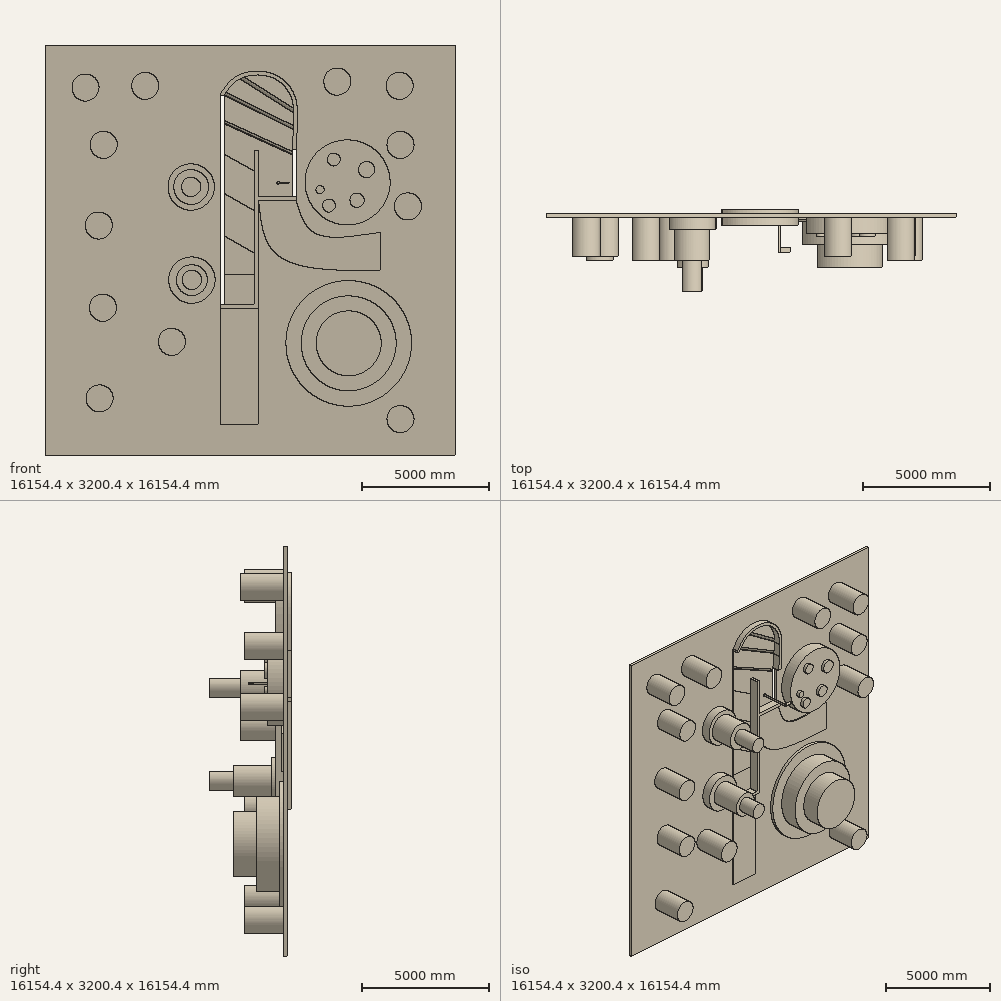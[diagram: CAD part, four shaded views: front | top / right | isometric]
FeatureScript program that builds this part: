
annotation { "Feature Type Name" : "Feature", "Feature Type Description" : "" }
export const myFeature = defineFeature(function(context is Context, id is Id, definition is map)
    precondition{}
    {
        {
            var Q0;
            Q0=qCreatedBy(makeId("Front.planeOp"),FACE);
            var sketch = newSketch(context, id + "F0", { "sketchPlane" : qUnion([Q0])});
            skLineSegment(sketch, "E0.bottom", {"start": v(12.17, -69.16) * mm, "end": v(1510.57, -69.16) * mm});
            skLineSegment(sketch, "E0.right", {"start": v(1510.57, -69.16) * mm, "end": v(1510.57, 6026.84) * mm});
            skLineSegment(sketch, "E1.top", {"start": v(1510.57, 4198.04) * mm, "end": v(2993.71, 4198.04) * mm});
            skLineSegment(sketch, "E1.left", {"start": v(1510.57, 6026.84) * mm, "end": v(1510.57, 4198.04) * mm});
            skCircle(sketch, "E2", {"center": v(2297.14, 4738.79) * mm, "radius": 64.77 * mm});
            skLineSegment(sketch, "E3", {"start": v(164.57, -69.16) * mm, "end": v(164.57, 8187.7) * mm});
            skFitSpline(sketch, "E4", {"points": [v(164.57, 8187.7) * mm, v(785.27, 8827.79) * mm, v(1987.86, 8905.37) * mm, v(2763.72, 8187.7) * mm, v(2899.5, 7217.86) * mm, v(2841.31, 6060.05) * mm], "startDerivative": vector(2756.52, 4024.76) * mm, "endDerivative": vector(-360.45, -5731.18) * mm});
            skLineSegment(sketch, "E5", {"start": v(2841.31, 6060.05) * mm, "end": v(2841.31, 4198.04) * mm});
            skLineSegment(sketch, "E6", {"start": v(164.57, 6656.24) * mm, "end": v(164.57, 7837.54) * mm});
            skLineSegment(sketch, "E7", {"start": v(2841.31, 5129.04) * mm, "end": v(2841.31, 4433.36) * mm});
            skLineSegment(sketch, "E8", {"start": v(164.57, 4316.15) * mm, "end": v(1358.17, 3632.72) * mm});
            skLineSegment(sketch, "E9", {"start": v(164.57, 5857.55) * mm, "end": v(1358.17, 5196.8) * mm});
            skLineSegment(sketch, "E10", {"start": v(164.57, 7060.6) * mm, "end": v(2841.31, 5838.75) * mm});
            skLineSegment(sketch, "E11", {"start": v(1510.57, 5112.44) * mm, "end": v(1510.57, 3545.46) * mm});
            skLineSegment(sketch, "E12", {"start": v(164.57, 4316.15) * mm, "end": v(164.57, 5857.55) * mm});
            skLineSegment(sketch, "E13", {"start": v(1510.57, 3545.46) * mm, "end": v(1510.57, 1872.48) * mm});
            skLineSegment(sketch, "E14", {"start": v(164.57, 4316.15) * mm, "end": v(164.57, 2643.18) * mm});
            skLineSegment(sketch, "E15", {"start": v(164.57, 8187.7) * mm, "end": v(2886.27, 6831.87) * mm});
            skLineSegment(sketch, "E16", {"start": v(2886.27, 6831.87) * mm, "end": v(2899.5, 7490.72) * mm});
            skLineSegment(sketch, "E17", {"start": v(2899.5, 7490.72) * mm, "end": v(785.27, 8827.79) * mm});
            skLineSegment(sketch, "E18", {"start": v(164.57, 2643.18) * mm, "end": v(1358.17, 1959.74) * mm});
            skLineSegment(sketch, "E19", {"start": v(164.57, 1113) * mm, "end": v(164.57, 2643.18) * mm});
            skLineSegment(sketch, "E20", {"start": v(1510.57, 1113) * mm, "end": v(1510.57, 1872.48) * mm});
            skLineSegment(sketch, "E21.0", {"start": v(1358.17, -69.16) * mm, "end": v(1358.17, 6026.84) * mm});
            skLineSegment(sketch, "E22", {"start": v(1358.17, 6026.84) * mm, "end": v(1510.57, 6026.84) * mm});
            skLineSegment(sketch, "E23.0", {"start": v(12.17, -69.16) * mm, "end": v(12.17, 8187.7) * mm});
            skLineSegment(sketch, "E24", {"start": v(12.17, 8187.7) * mm, "end": v(164.57, 8187.7) * mm});
            skFitSpline(sketch, "E25.0", {"points": [v(38.84, 8273.81) * mm, v(53.2, 8294.77) * mm, v(82.1, 8336.98) * mm, v(126.5, 8400.8) * mm, v(172.38, 8464.77) * mm, v(220.24, 8528.48) * mm, v(270.58, 8591.55) * mm, v(323.91, 8653.53) * mm, v(380.75, 8713.96) * mm, v(441.58, 8772.33) * mm, v(496, 8818.8) * mm, v(541.96, 8854.36) * mm, v(577.7, 8880.15) * mm, v(614.74, 8905) * mm, v(646.72, 8924.84) * mm, v(673, 8940.16) * mm, v(689.7, 8949.5) * mm, v(703.24, 8956.83) * mm, v(713.48, 8962.25) * mm, v(723.81, 8967.6) * mm, v(737.67, 8974.6) * mm, v(755.16, 8983.14) * mm, v(783.5, 8996.37) * mm, v(819.56, 9012.07) * mm, v(863.78, 9029.6) * mm, v(923.92, 9051.2) * mm, v(1001.14, 9074.97) * mm, v(1096.58, 9098.3) * mm, v(1194.28, 9116.45) * mm, v(1293.74, 9129.36) * mm, v(1394.44, 9136.97) * mm, v(1495.88, 9139.18) * mm, v(1597.55, 9135.89) * mm, v(1698.93, 9126.94) * mm, v(1799.49, 9112.17) * mm, v(1882.17, 9094.86) * mm, v(1939.23, 9080.03) * mm, v(1971.56, 9070.75) * mm, v(1995.67, 9063.4) * mm, v(2015.63, 9056.93) * mm, v(2031.51, 9051.55) * mm, v(2047.35, 9046.04) * mm, v(2067, 9038.9) * mm, v(2090.34, 9029.95) * mm, v(2113.45, 9020.62) * mm, v(2143.95, 9007.69) * mm, v(2181.48, 8990.6) * mm, v(2225.53, 8968.7) * mm, v(2282.93, 8937.7) * mm, v(2352.12, 8895.7) * mm, v(2430.92, 8840.47) * mm, v(2505.37, 8780.85) * mm, v(2575.33, 8717.2) * mm, v(2640.7, 8649.9) * mm, v(2701.34, 8579.3) * mm, v(2757.15, 8505.77) * mm, v(2799.53, 8442.32) * mm, v(2830.89, 8390.42) * mm, v(2853.12, 8350.96) * mm, v(2874.04, 8311.02) * mm, v(2890.38, 8277.36) * mm, v(2901.22, 8253.6) * mm, v(2907.25, 8240) * mm, v(2916.11, 8219.55) * mm, v(2928.76, 8188.76) * mm, v(2944.27, 8147.5) * mm, v(2958.48, 8106.07) * mm, v(2971.44, 8064.48) * mm, v(2987.14, 8008.84) * mm, v(3003.9, 7939) * mm, v(3019.9, 7854.89) * mm, v(3032.22, 7770.57) * mm, v(3041.3, 7686.13) * mm, v(3047.58, 7601.63) * mm, v(3051.48, 7517.12) * mm, v(3053.07, 7446.73) * mm, v(3053.56, 7390.46) * mm, v(3053.58, 7348.27) * mm, v(3053.3, 7306.11) * mm, v(3052.86, 7271) * mm, v(3052.4, 7242.94) * mm, v(3052.02, 7221.9) * mm, v(3051.59, 7200.87) * mm, v(3051.13, 7179.81) * mm, v(3050.63, 7158.73) * mm, v(3049.9, 7130.58) * mm, v(3048.53, 7081.24) * mm, v(3046.23, 7010.5) * mm, v(3042.96, 6925.23) * mm, v(3039.25, 6839.56) * mm, v(3035.13, 6753.5) * mm, v(3030.66, 6667.02) * mm, v(3024.3, 6551.2) * mm, v(3015.69, 6405.43) * mm, v(3004.69, 6228.9) * mm, v(2997.16, 6110.13) * mm, v(2993.4, 6050.48) * mm]});
            skLineSegment(sketch, "E26", {"start": v(38.84, 8273.81) * mm, "end": v(12.17, 8187.7) * mm});
            skLineSegment(sketch, "E27", {"start": v(2993.4, 6050.48) * mm, "end": v(2841.31, 6060.05) * mm});
            skLineSegment(sketch, "E28.0", {"start": v(2993.71, 6060.05) * mm, "end": v(2993.71, 4198.04) * mm});
            skPoint(sketch, "E29.orphan", {"position": v(3034.57, 4198.04) * mm});
            skLineSegment(sketch, "E30.0", {"start": v(1510.57, 4045.64) * mm, "end": v(2993.71, 4045.64) * mm});
            skLineSegment(sketch, "E31", {"start": v(2993.71, 4198.04) * mm, "end": v(2993.71, 4045.64) * mm});
            skLineSegment(sketch, "E32.0", {"start": v(12.17, -221.56) * mm, "end": v(1510.57, -221.56) * mm});
            skLineSegment(sketch, "E33", {"start": v(12.17, -69.16) * mm, "end": v(12.17, -221.56) * mm});
            skLineSegment(sketch, "E34", {"start": v(1510.57, -221.56) * mm, "end": v(1510.57, -69.16) * mm});
            skCircle(sketch, "E35", {"center": v(2297.14, 4738.79) * mm, "radius": 38.95 * mm});
            skLineSegment(sketch, "E36", {"start": v(12.17, -221.56) * mm, "end": v(12.17, -4793.56) * mm});
            skLineSegment(sketch, "E37", {"start": v(12.17, -4793.56) * mm, "end": v(1510.57, -4793.56) * mm});
            skLineSegment(sketch, "E38", {"start": v(1510.57, -4793.56) * mm, "end": v(1510.57, -221.56) * mm});
            skFitSpline(sketch, "E39", {"points": [v(1510.57, 4045.64) * mm, v(2242.66, 1900.94) * mm, v(6297.84, 1277.97) * mm], "startDerivative": vector(576.24, -5871.28) * mm, "endDerivative": vector(8604.1, 45.4) * mm});
            skLineSegment(sketch, "E40", {"start": v(6297.84, 1277.97) * mm, "end": v(6297.84, 2776.37) * mm});
            skFitSpline(sketch, "E41", {"points": [v(6297.84, 2776.37) * mm, v(3700.18, 2776.37) * mm, v(2993.71, 4045.64) * mm], "startDerivative": vector(-5366.67, -848.67) * mm, "endDerivative": vector(-1033.15, 3601.25) * mm});
            skLineSegment(sketch, "E42", {"start": v(164.57, 1113) * mm, "end": v(1358.17, 1113) * mm});
            skCircle(sketch, "E43", {"center": v(-1111.1, 901.55) * mm, "radius": 609.6 * mm});
            skCircle(sketch, "E44", {"center": v(-1111.1, 901.55) * mm, "radius": 914.4 * mm});
            skCircle(sketch, "E45", {"center": v(-1111.1, 901.55) * mm, "radius": 381 * mm});
            skCircle(sketch, "E46", {"center": v(-1139.74, 4569.72) * mm, "radius": 914.4 * mm});
            skCircle(sketch, "E47", {"center": v(-1139.74, 4569.72) * mm, "radius": 685.8 * mm});
            skCircle(sketch, "E48", {"center": v(-1139.74, 4569.72) * mm, "radius": 381 * mm});
            skLineSegment(sketch, "E49.bottom", {"start": v(-6882.14, 10147.6) * mm, "end": v(9272.26, 10147.6) * mm});
            skLineSegment(sketch, "E49.top", {"start": v(-6882.14, -6006.8) * mm, "end": v(9272.26, -6006.8) * mm});
            skLineSegment(sketch, "E49.left", {"start": v(-6882.14, 10147.6) * mm, "end": v(-6882.14, -6006.8) * mm});
            skLineSegment(sketch, "E49.right", {"start": v(9272.26, 10147.6) * mm, "end": v(9272.26, -6006.8) * mm});
            skCircle(sketch, "E50", {"center": v(5065.62, -1589.97) * mm, "radius": 2476.55 * mm});
            skCircle(sketch, "E51", {"center": v(5065.62, -1589.97) * mm, "radius": 1871.8 * mm});
            skCircle(sketch, "E52", {"center": v(5065.62, -1589.97) * mm, "radius": 1282.26 * mm});
            skCircle(sketch, "E53", {"center": v(-5304.9, 8488.5) * mm, "radius": 533.4 * mm});
            skCircle(sketch, "E54", {"center": v(-2947.24, 8554) * mm, "radius": 533.4 * mm});
            skCircle(sketch, "E55", {"center": v(4616.95, 8721.1) * mm, "radius": 533.4 * mm});
            skCircle(sketch, "E56", {"center": v(7072.86, 8554) * mm, "radius": 533.4 * mm});
            skCircle(sketch, "E57", {"center": v(-4584.5, 6229.08) * mm, "radius": 533.4 * mm});
            skCircle(sketch, "E58", {"center": v(7105.6, 6229.08) * mm, "radius": 533.4 * mm});
            skCircle(sketch, "E59", {"center": v(7400.31, 3805.92) * mm, "radius": 533.4 * mm});
            skCircle(sketch, "E60", {"center": v(-4780.98, 3052.77) * mm, "radius": 533.4 * mm});
            skCircle(sketch, "E61", {"center": v(-4617.25, -189.02) * mm, "radius": 533.4 * mm});
            skCircle(sketch, "E62", {"center": v(-1899.38, -1531.58) * mm, "radius": 533.4 * mm});
            skCircle(sketch, "E63", {"center": v(-4748.23, -3758.27) * mm, "radius": 533.4 * mm});
            skCircle(sketch, "E64", {"center": v(7105.6, -4576.9) * mm, "radius": 533.4 * mm});
            skSolve(sketch);
        }
        {
            var Q0;
            {var subQ0=sQuery(id+"F0.wireOp",EDGE,"E15");Q0=makeQuery(id+"F0.imprint","IMPRINT",FACE,{"disambiguationData":[TD([[makeQuery(id+"F0.imprint","IMPRINT",EDGE,{"derivedFrom":subQ0}),1.0]])]});}
            var Q1;
            Q1=makeQuery(id+"F0.imprint","IMPRINT",FACE,{"disambiguationData":[TD([[makeQuery(id+"F0.imprint","IMPRINT",EDGE,{"derivedFrom":sQuery(id+"F0.wireOp",EDGE,"E2")}),-1.0]])]});
            var Q2;
            {var subQ3=sQuery(id+"F0.wireOp",EDGE,"E10");Q2=makeQuery(id+"F0.imprint","IMPRINT",FACE,{"disambiguationData":[TD([[makeQuery(id+"F0.imprint","IMPRINT",EDGE,{"derivedFrom":subQ3}),1.0]])]});}
            var Q3;
            {var subQ11=sQuery(id+"F0.wireOp",EDGE,"E24");Q3=makeQuery(id+"F0.imprint","IMPRINT",FACE,{"disambiguationData":[TD([[makeQuery(id+"F0.imprint","IMPRINT",EDGE,{"derivedFrom":subQ11}),1.0]])]});}
            var Q4;
            {var subQ3=sQuery(id+"F0.wireOp",EDGE,"E7");Q4=makeQuery(id+"F0.imprint","IMPRINT",FACE,{"disambiguationData":[TD([[makeQuery(id+"F0.imprint","IMPRINT",EDGE,{"derivedFrom":subQ3}),1.0]])]});}
            var Q5;
            {var subQ0=sQuery(id+"F0.wireOp",EDGE,"E8");Q5=makeQuery(id+"F0.imprint","IMPRINT",FACE,{"disambiguationData":[TD([[makeQuery(id+"F0.imprint","IMPRINT",EDGE,{"derivedFrom":subQ0}),-1.0]])]});}
            var Q6;
            Q6=makeQuery(id+"F0.imprint","IMPRINT",FACE,{"disambiguationData":[TD([[makeQuery(id+"F0.imprint","IMPRINT",EDGE,{"derivedFrom":sQuery(id+"F0.wireOp",EDGE,"E32.0")}),1.0]])]});
            var Q7;
            {var subQ0=sQuery(id+"F0.wireOp",EDGE,"E17");Q7=makeQuery(id+"F0.imprint","IMPRINT",FACE,{"disambiguationData":[TD([[makeQuery(id+"F0.imprint","IMPRINT",EDGE,{"derivedFrom":subQ0}),-1.0]])]});}
            var Q8;
            {var subQ6=sQuery(id+"F0.wireOp",EDGE,"E18");Q8=makeQuery(id+"F0.imprint","IMPRINT",FACE,{"disambiguationData":[TD([[makeQuery(id+"F0.imprint","IMPRINT",EDGE,{"derivedFrom":subQ6}),-1.0]])]});}
            var Q9;
            {var subQ0=sQuery(id+"F0.wireOp",EDGE,"E8");Q9=makeQuery(id+"F0.imprint","IMPRINT",FACE,{"disambiguationData":[TD([[makeQuery(id+"F0.imprint","IMPRINT",EDGE,{"derivedFrom":subQ0}),1.0]])]});}
            var Q10;
            {var subQ0=sQuery(id+"F0.wireOp",EDGE,"E30.0");Q10=makeQuery(id+"F0.imprint","IMPRINT",FACE,{"disambiguationData":[TD([[makeQuery(id+"F0.imprint","IMPRINT",EDGE,{"derivedFrom":subQ0}),1.0]])]});}
            var Q11;
            {var subQ1=sQuery(id+"F0.wireOp",EDGE,"E12");Q11=makeQuery(id+"F0.imprint","IMPRINT",FACE,{"disambiguationData":[TD([[makeQuery(id+"F0.imprint","IMPRINT",EDGE,{"derivedFrom":subQ1}),1.0]])]});}
            var Q12;
            {var subQ6=sQuery(id+"F0.wireOp",EDGE,"E0.right");Q12=makeQuery(id+"F0.imprint","IMPRINT",FACE,{"disambiguationData":[TD([[makeQuery(id+"F0.imprint","IMPRINT",EDGE,{"derivedFrom":subQ6}),1.0]])]});}
            var Q13;
            {var subQ0=sQuery(id+"F0.wireOp",EDGE,"E16");Q13=makeQuery(id+"F0.imprint","IMPRINT",FACE,{"disambiguationData":[TD([[makeQuery(id+"F0.imprint","IMPRINT",EDGE,{"derivedFrom":subQ0}),-1.0]])]});}
            var Q14;
            Q14=makeQuery(id+"F0.imprint","IMPRINT",FACE,{"disambiguationData":[TD([[makeQuery(id+"F0.imprint","IMPRINT",EDGE,{"derivedFrom":sQuery(id+"F0.wireOp",EDGE,"E2")}),1.0]])]});
            extrude(context, id + "F1", {"entities" : qUnion([Q0, Q1, Q2, Q3, Q4, Q5, Q6, Q7, Q8, Q9, Q10, Q11, Q12, Q13, Q14]), "oppositeDirection" : true, "depth" : 152.4 * mm});
        }
        {
            var Q0;
            {var subQ0=sQuery(id+"F0.wireOp",EDGE,"E17");Q0=makeQuery(id+"F0.imprint","IMPRINT",FACE,{"disambiguationData":[TD([[makeQuery(id+"F0.imprint","IMPRINT",EDGE,{"derivedFrom":subQ0}),-1.0]])]});}
            var Q1;
            {var subQ3=sQuery(id+"F0.wireOp",EDGE,"E10");Q1=makeQuery(id+"F0.imprint","IMPRINT",FACE,{"disambiguationData":[TD([[makeQuery(id+"F0.imprint","IMPRINT",EDGE,{"derivedFrom":subQ3}),1.0]])]});}
            var Q2;
            {var subQ0=sQuery(id+"F0.wireOp",EDGE,"E8");Q2=makeQuery(id+"F0.imprint","IMPRINT",FACE,{"disambiguationData":[TD([[makeQuery(id+"F0.imprint","IMPRINT",EDGE,{"derivedFrom":subQ0}),1.0]])]});}
            var Q3;
            {var subQ6=sQuery(id+"F0.wireOp",EDGE,"E18");Q3=makeQuery(id+"F0.imprint","IMPRINT",FACE,{"disambiguationData":[TD([[makeQuery(id+"F0.imprint","IMPRINT",EDGE,{"derivedFrom":subQ6}),-1.0]])]});}
            extrude(context, id + "F2", {"entities" : qUnion([Q0, Q1, Q2, Q3]), "depth" : 25.4 * mm});
        }
        {
            var Q0;
            {var subQ0=sQuery(id+"F0.wireOp",EDGE,"E15");Q0=makeQuery(id+"F0.imprint","IMPRINT",FACE,{"disambiguationData":[TD([[makeQuery(id+"F0.imprint","IMPRINT",EDGE,{"derivedFrom":subQ0}),1.0]])]});}
            var Q1;
            Q1=makeQuery(id+"F0.imprint","IMPRINT",FACE,{"disambiguationData":[TD([[makeQuery(id+"F0.imprint","IMPRINT",EDGE,{"derivedFrom":sQuery(id+"F0.wireOp",EDGE,"E2")}),-1.0]])]});
            var Q2;
            {var subQ0=sQuery(id+"F0.wireOp",EDGE,"E8");Q2=makeQuery(id+"F0.imprint","IMPRINT",FACE,{"disambiguationData":[TD([[makeQuery(id+"F0.imprint","IMPRINT",EDGE,{"derivedFrom":subQ0}),-1.0]])]});}
            extrude(context, id + "F3", {"entities" : qUnion([Q0, Q1, Q2]), "depth" : 25.4 * mm});
        }
        {
            var Q0;
            Q0=makeQuery(id+"F0.imprint","IMPRINT",FACE,{"disambiguationData":[TD([[makeQuery(id+"F0.imprint","IMPRINT",EDGE,{"derivedFrom":sQuery(id+"F0.wireOp",EDGE,"E2")}),1.0]])]});
            extrude(context, id + "F4", {"entities" : qUnion([Q0]), "operationType" : NewBodyOperationType.REMOVE, "oppositeDirection" : true, "depth" : 76.2 * mm});
        }
        {
            var Q0;
            {var subQ1=sQuery(id+"F0.wireOp",EDGE,"E12");Q0=makeQuery(id+"F0.imprint","IMPRINT",FACE,{"disambiguationData":[TD([[makeQuery(id+"F0.imprint","IMPRINT",EDGE,{"derivedFrom":subQ1}),1.0]])]});}
            var Q1;
            {var subQ6=sQuery(id+"F0.wireOp",EDGE,"E0.right");Q1=makeQuery(id+"F0.imprint","IMPRINT",FACE,{"disambiguationData":[TD([[makeQuery(id+"F0.imprint","IMPRINT",EDGE,{"derivedFrom":subQ6}),1.0]])]});}
            var Q2;
            Q2=makeQuery(id+"F0.imprint","IMPRINT",FACE,{"disambiguationData":[TD([[makeQuery(id+"F0.imprint","IMPRINT",EDGE,{"derivedFrom":sQuery(id+"F0.wireOp",EDGE,"E32.0")}),1.0]])]});
            var Q3;
            {var subQ11=sQuery(id+"F0.wireOp",EDGE,"E24");Q3=makeQuery(id+"F0.imprint","IMPRINT",FACE,{"disambiguationData":[TD([[makeQuery(id+"F0.imprint","IMPRINT",EDGE,{"derivedFrom":subQ11}),1.0]])]});}
            var Q4;
            {var subQ3=sQuery(id+"F0.wireOp",EDGE,"E7");Q4=makeQuery(id+"F0.imprint","IMPRINT",FACE,{"disambiguationData":[TD([[makeQuery(id+"F0.imprint","IMPRINT",EDGE,{"derivedFrom":subQ3}),1.0]])]});}
            var Q5;
            {var subQ0=sQuery(id+"F0.wireOp",EDGE,"E30.0");Q5=makeQuery(id+"F0.imprint","IMPRINT",FACE,{"disambiguationData":[TD([[makeQuery(id+"F0.imprint","IMPRINT",EDGE,{"derivedFrom":subQ0}),1.0]])]});}
            extrude(context, id + "F5", {"entities" : qUnion([Q0, Q1, Q2, Q3, Q4, Q5]), "depth" : 457.2 * mm});
        }
        {
            var Q0;
            Q0=makeQuery(id+"F0.imprint","IMPRINT",FACE,{"disambiguationData":[TD([[makeQuery(id+"F0.imprint","IMPRINT",EDGE,{"derivedFrom":sQuery(id+"F0.wireOp",EDGE,"E35")}),1.0]])]});
            extrude(context, id + "F6", {"entities" : qUnion([Q0]), "depth" : 1524 * mm});
        }
        {
            var Q0;
            Q0=makeQuery(id+"F0.imprint","IMPRINT",FACE,{"disambiguationData":[TD([[makeQuery(id+"F0.imprint","IMPRINT",EDGE,{"derivedFrom":sQuery(id+"F0.wireOp",EDGE,"E32.0")}),-1.0]])]});
            var Q1;
            Q1=makeQuery(id+"F0.imprint","IMPRINT",FACE,{"disambiguationData":[TD([[makeQuery(id+"F0.imprint","IMPRINT",EDGE,{"derivedFrom":sQuery(id+"F0.wireOp",EDGE,"E30.0")}),-1.0]])]});
            extrude(context, id + "F7", {"entities" : qUnion([Q0, Q1]), "operationType" : NewBodyOperationType.ADD, "depth" : 152.4 * mm});
        }
        {
            var Q0;
            {var subQ5=sQuery(id+"F0.wireOp",EDGE,"E42");Q0=makeQuery(id+"F0.imprint","IMPRINT",FACE,{"disambiguationData":[TD([[makeQuery(id+"F0.imprint","IMPRINT",EDGE,{"derivedFrom":subQ5}),-1.0]])]});}
            extrude(context, id + "F8", {"entities" : qUnion([Q0]), "depth" : 25.3 * mm});
        }
        {
            var Q0;
            Q0=makeQuery(id+"F0.imprint","IMPRINT",FACE,{"disambiguationData":[TD([[makeQuery(id+"F0.imprint","IMPRINT",EDGE,{"derivedFrom":sQuery(id+"F0.wireOp",EDGE,"E43")}),-1.0]])]});
            extrude(context, id + "F9", {"entities" : qUnion([Q0]), "depth" : 609.6 * mm});
        }
        {
            var Q0;
            Q0=makeQuery(id+"F0.imprint","IMPRINT",FACE,{"disambiguationData":[TD([[makeQuery(id+"F0.imprint","IMPRINT",EDGE,{"derivedFrom":sQuery(id+"F0.wireOp",EDGE,"E43")}),1.0]])]});
            extrude(context, id + "F10", {"entities" : qUnion([Q0]), "depth" : 2133.6 * mm});
        }
        {
            var Q0;
            Q0=makeQuery(id+"F0.imprint","IMPRINT",FACE,{"disambiguationData":[TD([[makeQuery(id+"F0.imprint","IMPRINT",EDGE,{"derivedFrom":sQuery(id+"F0.wireOp",EDGE,"E45")}),1.0]])]});
            extrude(context, id + "F11", {"entities" : qUnion([Q0]), "depth" : 152.4 * mm});
        }
        {
            var Q0;
            Q0=makeQuery(id+"F0.imprint","IMPRINT",FACE,{"disambiguationData":[TD([[makeQuery(id+"F0.imprint","IMPRINT",EDGE,{"derivedFrom":sQuery(id+"F0.wireOp",EDGE,"E45")}),1.0]])]});
            extrude(context, id + "F12", {"entities" : qUnion([Q0]), "operationType" : NewBodyOperationType.ADD, "depth" : 3048 * mm});
        }
        {
            var Q0;
            Q0=makeQuery(id+"F6.opExtrude","CAP_EDGE",EDGE,{"disambiguationData":[OSD([sQuery(id+"F0.wireOp",EDGE,"E35")])],"isStart":false});
            cPlane(context, id + "F13", {"entities" : qUnion([Q0]), "cplaneType" : CPlaneType.LINE_ANGLE, "offset" : 0 * mm, "angle" : 360 * degree, "width" : 152.4 * mm, "height" : 152.4 * mm});
        }
        {
            var Q0;
            Q0=qCreatedBy(id+"F13.planeOp",FACE);
            var sketch = newSketch(context, id + "F14", { "sketchPlane" : qUnion([Q0])});
            skLineSegment(sketch, "E65.bottom", {"start": v(2336.03, 1519.4) * mm, "end": v(2717.1, 1519.4) * mm});
            skLineSegment(sketch, "E65.top", {"start": v(2336.03, 1337.46) * mm, "end": v(2717.1, 1337.46) * mm});
            skLineSegment(sketch, "E65.left", {"start": v(2336.03, 1519.4) * mm, "end": v(2336.03, 1337.46) * mm});
            skLineSegment(sketch, "E65.right", {"start": v(2717.1, 1519.4) * mm, "end": v(2717.1, 1337.46) * mm});
            skSolve(sketch);
        }
        {
            var Q0;
            Q0=makeQuery(id+"F14.imprint","IMPRINT",FACE,{"disambiguationData":[TD([[makeQuery(id+"F14.imprint","IMPRINT",EDGE,{"derivedFrom":sQuery(id+"F14.wireOp",EDGE,"E65.bottom")}),-1.0]])]});
            extrude(context, id + "F15", {"entities" : qUnion([Q0]), "depth" : 30.48 * mm});
        }
        {
            var Q0;
            Q0=makeQuery(id+"F0.imprint","IMPRINT",FACE,{"disambiguationData":[TD([[makeQuery(id+"F0.imprint","IMPRINT",EDGE,{"derivedFrom":sQuery(id+"F0.wireOp",EDGE,"E46")}),1.0]])]});
            extrude(context, id + "F16", {"entities" : qUnion([Q0]), "depth" : 609.6 * mm});
        }
        {
            var Q0;
            Q0=makeQuery(id+"F0.imprint","IMPRINT",FACE,{"disambiguationData":[TD([[makeQuery(id+"F0.imprint","IMPRINT",EDGE,{"derivedFrom":sQuery(id+"F0.wireOp",EDGE,"E47")}),1.0]])]});
            extrude(context, id + "F17", {"entities" : qUnion([Q0]), "operationType" : NewBodyOperationType.ADD, "depth" : 1828.8 * mm});
        }
        {
            var Q0;
            Q0=makeQuery(id+"F0.imprint","IMPRINT",FACE,{"disambiguationData":[TD([[makeQuery(id+"F0.imprint","IMPRINT",EDGE,{"derivedFrom":sQuery(id+"F0.wireOp",EDGE,"E48")}),1.0]])]});
            extrude(context, id + "F18", {"entities" : qUnion([Q0]), "operationType" : NewBodyOperationType.ADD, "depth" : 3048 * mm});
        }
        {
            var Q0;
            Q0=makeQuery(id+"F0.imprint","IMPRINT",FACE,{"disambiguationData":[TD([[makeQuery(id+"F0.imprint","IMPRINT",EDGE,{"derivedFrom":sQuery(id+"F0.wireOp",EDGE,"E0.right")}),-1.0]])]});
            extrude(context, id + "F19", {"entities" : qUnion([Q0]), "depth" : 152.4 * mm});
        }
        {
            var Q0;
            Q0=makeQuery(id+"F0.imprint","IMPRINT",FACE,{"disambiguationData":[TD([[makeQuery(id+"F0.imprint","IMPRINT",EDGE,{"derivedFrom":sQuery(id+"F0.wireOp",EDGE,"E30.0")}),-1.0]])]});
            var Q1;
            Q1=makeQuery(id+"F0.imprint","IMPRINT",FACE,{"disambiguationData":[TD([[makeQuery(id+"F0.imprint","IMPRINT",EDGE,{"derivedFrom":sQuery(id+"F0.wireOp",EDGE,"E32.0")}),-1.0]])]});
            extrude(context, id + "F20", {"entities" : qUnion([Q0, Q1]), "depth" : 228.6 * mm});
        }
        {
            var Q0;
            Q0=makeQuery(id+"F19.opExtrude","CAP_FACE",FACE,{"disambiguationData":[OSD([sQuery(id+"F0.wireOp",EDGE,"E0.right"),sQuery(id+"F0.wireOp",EDGE,"E11"),sQuery(id+"F0.wireOp",EDGE,"E13"),sQuery(id+"F0.wireOp",EDGE,"E20"),sQuery(id+"F0.wireOp",EDGE,"E23.0"),sQuery(id+"F0.wireOp",EDGE,"E25.0"),sQuery(id+"F0.wireOp",EDGE,"E26"),sQuery(id+"F0.wireOp",EDGE,"E28.0"),sQuery(id+"F0.wireOp",EDGE,"E31"),sQuery(id+"F0.wireOp",EDGE,"E33"),sQuery(id+"F0.wireOp",EDGE,"E34"),sQuery(id+"F0.wireOp",EDGE,"E36"),sQuery(id+"F0.wireOp",EDGE,"E37"),sQuery(id+"F0.wireOp",EDGE,"E38"),sQuery(id+"F0.wireOp",EDGE,"E39"),sQuery(id+"F0.wireOp",EDGE,"E40"),sQuery(id+"F0.wireOp",EDGE,"E41"),sQuery(id+"F0.wireOp",EDGE,"E44"),sQuery(id+"F0.wireOp",EDGE,"E46"),sQuery(id+"F0.wireOp",EDGE,"E49.bottom"),sQuery(id+"F0.wireOp",EDGE,"E49.top"),sQuery(id+"F0.wireOp",EDGE,"E49.left"),sQuery(id+"F0.wireOp",EDGE,"E49.right")])],"isStart":false});
            var sketch = newSketch(context, id + "F21", { "sketchPlane" : qUnion([Q0])});
            skCircle(sketch, "E66", {"center": v(5021.96, 4752.78) * mm, "radius": 1676.4 * mm});
            skCircle(sketch, "E67", {"center": v(4478.87, 5650.97) * mm, "radius": 252.4 * mm});
            skCircle(sketch, "E68", {"center": v(5397.95, 4045.64) * mm, "radius": 283.3 * mm});
            skCircle(sketch, "E69", {"center": v(5773.93, 5254.1) * mm, "radius": 318.84 * mm});
            skCircle(sketch, "E70", {"center": v(3935.78, 4460.34) * mm, "radius": 163.14 * mm});
            skCircle(sketch, "E71", {"center": v(4290.88, 3833.7) * mm, "radius": 254.97 * mm});
            skSolve(sketch);
        }
        {
            var Q0;
            Q0=makeQuery(id+"F21.imprint","IMPRINT",FACE,{"disambiguationData":[TD([[makeQuery(id+"F21.imprint","IMPRINT",EDGE,{"derivedFrom":sQuery(id+"F21.wireOp",EDGE,"E67")}),1.0]])]});
            var Q1;
            Q1=makeQuery(id+"F21.imprint","IMPRINT",FACE,{"disambiguationData":[TD([[makeQuery(id+"F21.imprint","IMPRINT",EDGE,{"derivedFrom":sQuery(id+"F21.wireOp",EDGE,"E70")}),1.0]])]});
            var Q2;
            Q2=makeQuery(id+"F21.imprint","IMPRINT",FACE,{"disambiguationData":[TD([[makeQuery(id+"F21.imprint","IMPRINT",EDGE,{"derivedFrom":sQuery(id+"F21.wireOp",EDGE,"E71")}),1.0]])]});
            var Q3;
            Q3=makeQuery(id+"F21.imprint","IMPRINT",FACE,{"disambiguationData":[TD([[makeQuery(id+"F21.imprint","IMPRINT",EDGE,{"derivedFrom":sQuery(id+"F21.wireOp",EDGE,"E68")}),1.0]])]});
            var Q4;
            Q4=makeQuery(id+"F21.imprint","IMPRINT",FACE,{"disambiguationData":[TD([[makeQuery(id+"F21.imprint","IMPRINT",EDGE,{"derivedFrom":sQuery(id+"F21.wireOp",EDGE,"E69")}),1.0]])]});
            extrude(context, id + "F22", {"entities" : qUnion([Q0, Q1, Q2, Q3, Q4]), "depth" : 762 * mm});
        }
        {
            var Q0;
            Q0=makeQuery(id+"F21.imprint","IMPRINT",FACE,{"disambiguationData":[TD([[makeQuery(id+"F21.imprint","IMPRINT",EDGE,{"derivedFrom":sQuery(id+"F21.wireOp",EDGE,"E66")}),1.0]])]});
            extrude(context, id + "F23", {"entities" : qUnion([Q0]), "depth" : 609.6 * mm});
        }
        {
            var Q0;
            Q0=makeQuery(id+"F2.opExtrude","CAP_FACE",FACE,{"disambiguationData":[OSD([sQuery(id+"F0.wireOp",EDGE,"E3"),sQuery(id+"F0.wireOp",EDGE,"E4"),sQuery(id+"F0.wireOp",EDGE,"E5"),sQuery(id+"F0.wireOp",EDGE,"E6"),sQuery(id+"F0.wireOp",EDGE,"E10"),sQuery(id+"F0.wireOp",EDGE,"E15")])],"isStart":false});
            var Q1;
            Q1=makeQuery(id+"F3.opExtrude","CAP_FACE",FACE,{"disambiguationData":[OSD([sQuery(id+"F0.wireOp",EDGE,"E4"),sQuery(id+"F0.wireOp",EDGE,"E15"),sQuery(id+"F0.wireOp",EDGE,"E16"),sQuery(id+"F0.wireOp",EDGE,"E17")])],"isStart":false});
            var Q2;
            Q2=makeQuery(id+"F2.opExtrude","CAP_FACE",FACE,{"disambiguationData":[OSD([sQuery(id+"F0.wireOp",EDGE,"E4"),sQuery(id+"F0.wireOp",EDGE,"E17")])],"isStart":false});
            chamfer(context, id + "F24", {"entities" : qUnion([Q0, Q1, Q2]), "width" : 304.8 * mm, "tangentPropagation" : true});
        }
        {
            var Q0;
            {var subQ3=sQuery(id+"F0.wireOp",EDGE,"E10");Q0=makeQuery(id+"F0.imprint","IMPRINT",FACE,{"disambiguationData":[TD([[makeQuery(id+"F0.imprint","IMPRINT",EDGE,{"derivedFrom":subQ3}),1.0]])]});}
            extrude(context, id + "F25", {"entities" : qUnion([Q0]), "depth" : 60.96 * mm});
        }
        {
            var Q0;
            {var subQ0=sQuery(id+"F0.wireOp",EDGE,"E15");Q0=makeQuery(id+"F0.imprint","IMPRINT",FACE,{"disambiguationData":[TD([[makeQuery(id+"F0.imprint","IMPRINT",EDGE,{"derivedFrom":subQ0}),1.0]])]});}
            extrude(context, id + "F26", {"entities" : qUnion([Q0]), "depth" : 91.44 * mm});
        }
        {
            var Q0;
            {var subQ0=sQuery(id+"F0.wireOp",EDGE,"E17");Q0=makeQuery(id+"F0.imprint","IMPRINT",FACE,{"disambiguationData":[TD([[makeQuery(id+"F0.imprint","IMPRINT",EDGE,{"derivedFrom":subQ0}),-1.0]])]});}
            extrude(context, id + "F27", {"entities" : qUnion([Q0]), "depth" : 121.92 * mm});
        }
        {
            var Q0;
            Q0=makeQuery(id+"F25.opExtrude","CAP_EDGE",EDGE,{"disambiguationData":[OSD([sQuery(id+"F0.wireOp",EDGE,"E10")])],"isStart":false});
            var Q1;
            Q1=makeQuery(id+"F26.opExtrude","CAP_EDGE",EDGE,{"disambiguationData":[OSD([sQuery(id+"F0.wireOp",EDGE,"E15")])],"isStart":false});
            var Q2;
            Q2=makeQuery(id+"F27.opExtrude","CAP_EDGE",EDGE,{"disambiguationData":[OSD([sQuery(id+"F0.wireOp",EDGE,"E17")])],"isStart":false});
            fillet(context, id + "F28", {"entities" : qUnion([Q0, Q1, Q2]), "radius" : 152.4 * mm, "tangentPropagation" : true, "allowEdgeOverflow" : false});
        }
        {
            var Q0;
            Q0=makeQuery(id+"F0.imprint","IMPRINT",FACE,{"disambiguationData":[TD([[makeQuery(id+"F0.imprint","IMPRINT",EDGE,{"derivedFrom":sQuery(id+"F0.wireOp",EDGE,"E50")}),1.0]])]});
            extrude(context, id + "F29", {"entities" : qUnion([Q0]), "operationType" : NewBodyOperationType.ADD, "depth" : 304.8 * mm});
        }
        {
            var Q0;
            Q0=makeQuery(id+"F0.imprint","IMPRINT",FACE,{"disambiguationData":[TD([[makeQuery(id+"F0.imprint","IMPRINT",EDGE,{"derivedFrom":sQuery(id+"F0.wireOp",EDGE,"E51")}),1.0]])]});
            extrude(context, id + "F30", {"entities" : qUnion([Q0]), "depth" : 1219.2 * mm});
        }
        {
            var Q0;
            Q0=makeQuery(id+"F0.imprint","IMPRINT",FACE,{"disambiguationData":[TD([[makeQuery(id+"F0.imprint","IMPRINT",EDGE,{"derivedFrom":sQuery(id+"F0.wireOp",EDGE,"E52")}),1.0]])]});
            extrude(context, id + "F31", {"entities" : qUnion([Q0]), "depth" : 2133.6 * mm});
        }
        {
            var Q0;
            Q0=makeQuery(id+"F0.imprint","IMPRINT",FACE,{"disambiguationData":[TD([[makeQuery(id+"F0.imprint","IMPRINT",EDGE,{"derivedFrom":sQuery(id+"F0.wireOp",EDGE,"E63")}),1.0]])]});
            var Q1;
            Q1=makeQuery(id+"F0.imprint","IMPRINT",FACE,{"disambiguationData":[TD([[makeQuery(id+"F0.imprint","IMPRINT",EDGE,{"derivedFrom":sQuery(id+"F0.wireOp",EDGE,"E61")}),1.0]])]});
            var Q2;
            Q2=makeQuery(id+"F0.imprint","IMPRINT",FACE,{"disambiguationData":[TD([[makeQuery(id+"F0.imprint","IMPRINT",EDGE,{"derivedFrom":sQuery(id+"F0.wireOp",EDGE,"E57")}),1.0]])]});
            var Q3;
            Q3=makeQuery(id+"F0.imprint","IMPRINT",FACE,{"disambiguationData":[TD([[makeQuery(id+"F0.imprint","IMPRINT",EDGE,{"derivedFrom":sQuery(id+"F0.wireOp",EDGE,"E53")}),1.0]])]});
            var Q4;
            Q4=makeQuery(id+"F0.imprint","IMPRINT",FACE,{"disambiguationData":[TD([[makeQuery(id+"F0.imprint","IMPRINT",EDGE,{"derivedFrom":sQuery(id+"F0.wireOp",EDGE,"E55")}),1.0]])]});
            var Q5;
            Q5=makeQuery(id+"F0.imprint","IMPRINT",FACE,{"disambiguationData":[TD([[makeQuery(id+"F0.imprint","IMPRINT",EDGE,{"derivedFrom":sQuery(id+"F0.wireOp",EDGE,"E58")}),1.0]])]});
            var Q6;
            Q6=makeQuery(id+"F0.imprint","IMPRINT",FACE,{"disambiguationData":[TD([[makeQuery(id+"F0.imprint","IMPRINT",EDGE,{"derivedFrom":sQuery(id+"F0.wireOp",EDGE,"E64")}),1.0]])]});
            extrude(context, id + "F32", {"entities" : qUnion([Q0, Q1, Q2, Q3, Q4, Q5, Q6]), "depth" : 1676.4 * mm});
        }
        {
            var Q0;
            Q0=makeQuery(id+"F21.imprint","IMPRINT",FACE,{"disambiguationData":[TD([[makeQuery(id+"F21.imprint","IMPRINT",EDGE,{"derivedFrom":makeQuery(id+"F19.opExtrude","CAP_EDGE",EDGE,{"disambiguationData":[OSD([sQuery(id+"F0.wireOp",EDGE,"E60")])],"isStart":false})}),1.0]])]});
            var Q1;
            Q1=makeQuery(id+"F21.imprint","IMPRINT",FACE,{"disambiguationData":[TD([[makeQuery(id+"F21.imprint","IMPRINT",EDGE,{"derivedFrom":makeQuery(id+"F19.opExtrude","CAP_EDGE",EDGE,{"disambiguationData":[OSD([sQuery(id+"F0.wireOp",EDGE,"E62")])],"isStart":false})}),1.0]])]});
            var Q2;
            Q2=makeQuery(id+"F21.imprint","IMPRINT",FACE,{"disambiguationData":[TD([[makeQuery(id+"F21.imprint","IMPRINT",EDGE,{"derivedFrom":makeQuery(id+"F19.opExtrude","CAP_EDGE",EDGE,{"disambiguationData":[OSD([sQuery(id+"F0.wireOp",EDGE,"E54")])],"isStart":false})}),1.0]])]});
            var Q3;
            Q3=makeQuery(id+"F21.imprint","IMPRINT",FACE,{"disambiguationData":[TD([[makeQuery(id+"F21.imprint","IMPRINT",EDGE,{"derivedFrom":makeQuery(id+"F19.opExtrude","CAP_EDGE",EDGE,{"disambiguationData":[OSD([sQuery(id+"F0.wireOp",EDGE,"E56")])],"isStart":false})}),1.0]])]});
            var Q4;
            Q4=makeQuery(id+"F21.imprint","IMPRINT",FACE,{"disambiguationData":[TD([[makeQuery(id+"F21.imprint","IMPRINT",EDGE,{"derivedFrom":makeQuery(id+"F19.opExtrude","CAP_EDGE",EDGE,{"disambiguationData":[OSD([sQuery(id+"F0.wireOp",EDGE,"E59")])],"isStart":false})}),1.0]])]});
            extrude(context, id + "F33", {"entities" : qUnion([Q0, Q1, Q2, Q3, Q4]), "depth" : 1676.4 * mm});
        }
    });
